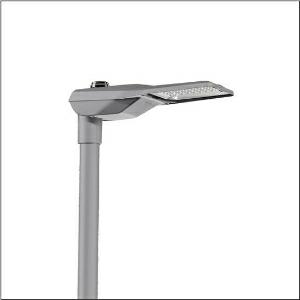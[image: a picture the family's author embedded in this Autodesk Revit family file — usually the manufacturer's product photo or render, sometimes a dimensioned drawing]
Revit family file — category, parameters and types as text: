
# Revit family: streetlight_sl_21_mini___st0_5a_5xe6b47n08hb_7d81
name_source: partatom
category: Lighting Fixtures
units: mm (PartAtom-declared; Revit-internal decimal feet)

## family parameters
Cut with Voids When Loaded = No
Host = Face
Light Source = No
Part Type = Normal
Room Calculation Point = No
Round Connector Dimension = Use Diameter
Shared = No

## types (1)
- --- (1 x LED, 9430 lm, 66 W, 4000K)
    Apparent Load = 66 VA
    CIE Flux Codes = 41 75 97 100 100
    Color Rendering = 70
    Color Temperature = 4000K
    Default Elevation = 1800 mm
    Description = Streetlight SL 21 mini, mast luminaire, primary light control with lens, of PMMA, primary optical cover: cover, of toughened safety glass, transparent, light distribution: ST0.5a, light emission: direct distribution, primary light characteristic: asymmetric, installation type: side-entry, LED, 3G 1.5mm², High Power LED, rated luminous flux: 9.430lm, luminous efficacy: 143lm/W, light colour: 740, colour temperature: 4000K, control gear: NEMA (7pin), control: overheat protection, pre-setting: linear dimming characteristic, constant luminous flux control, time-dependent luminous flux control, flexible luminous flux parameterisation, mains connection: 230..240V, AC, 50/60Hz, connection cable pre-assembled, cable length: 8,5m, wiring characteristics: H07RN-F, start of lifetime: 66W, end of service life: 69W, reduction: 30W, luminaire housing, of diecast aluminium (EN AC-44300), powder-coated, Siteco® metallic grey (DB 702S), corrosivity category C5 mid according to DIN EN ISO 12944, multi-level sealing system, sealing non-destructively replaceable, inclination adjustable: 0°, 5°, 10°, 15°, length: 628mm, width: 235mm, height: 110mm, spigot size: 42mm (side-entry), mounting height: 4..8m, protection rating (complete): IP66, insulation class (complete): insulation class I (protective earthing), certification: CE, ENEC, ENEC+, VDE, impact resistance: IK10, permissible operating ambient temperature for outdoor applications: -40..+50°C, standard-compliant lighting for roads and squares, packaging unit: 1 piece

Light Distribution: ST0.5a
    Height = 110 mm
    Lamp = 1 x LED
    Lamp Light Flux = 9430 lm
    Lamp Power = 66 W
    Lamp count = 1
    Length = 625 mm
    Luminous efficacy = 143 lm/W
    Manufacturer = Siteco
    ModVariant = No
    Model = 5XE6B47N08HB
    Number of Poles = 1
    OnlyDefault = Yes
    Power Factor = 1
    Product Name = Streetlight SL 21 mini | ST0.5a
    Product group = mast luminaire | pylon top
    ProductGroupID = 6100
    Protection Class = Protection class I
    Protection Degree = IP 66
    RLX_Detail_Level = 1
    RLX_Emergency_Light_Flux = 0 lm
    RLX_Emergency_Type = 0
    RLX_Emergency_Type_DB = No
    RlxData = <blob elided: 37177 chars, md5=fe432a10>
    Socket = socket
    Standby Power = 0 W
    System Light Flux = 9430 lm
    System Power = 66 W
    Type Comments = factory setting: luminous flux: 100 % | dim-lin: 254 | 670 mA
    Type Image = l_1294379.jpg
    URL = http://relux.com
    VarID = @adj_137418
    Voltage = 0 V
    Weight = 0.00 kg
    Width = 234 mm

## geometry (parser evidence)
native form markers: Blend x4, Sweep x12
no freeform markers — native parametric forms only
